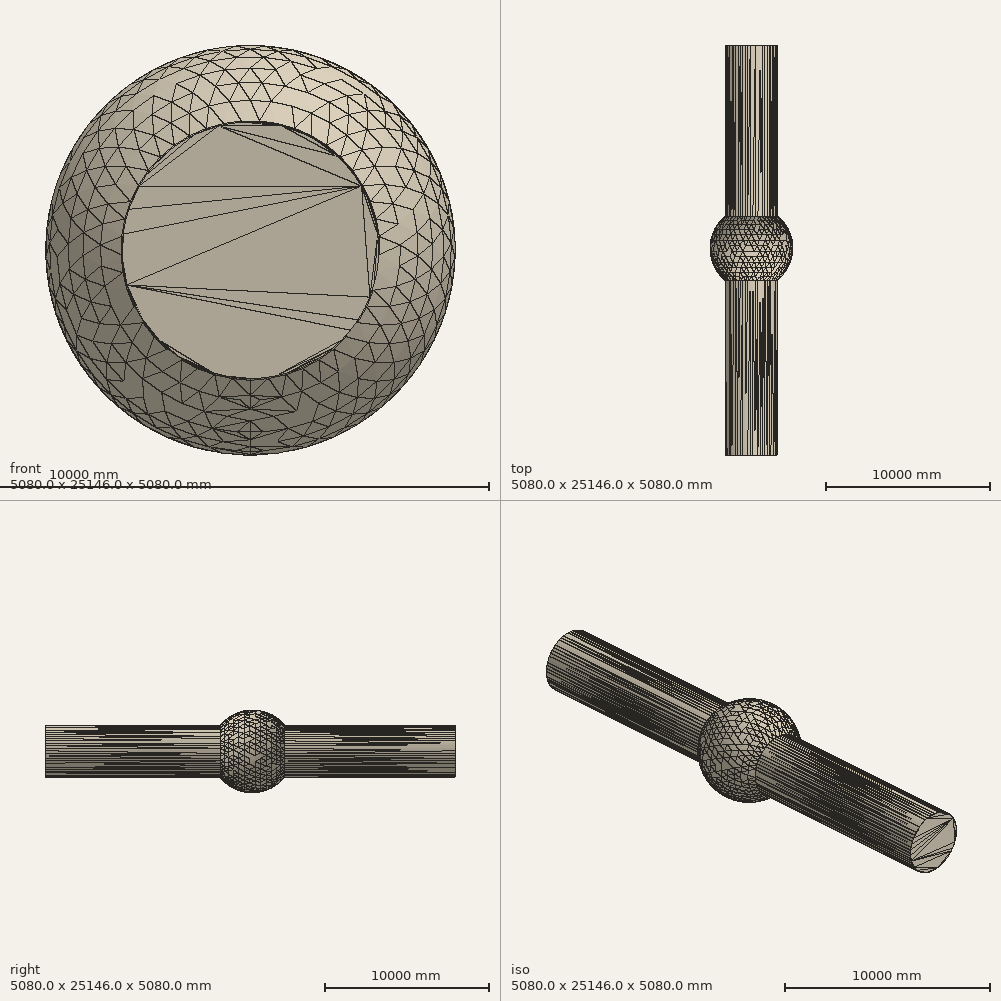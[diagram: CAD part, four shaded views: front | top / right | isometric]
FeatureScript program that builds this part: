
annotation { "Feature Type Name" : "Feature", "Feature Type Description" : "" }
export const myFeature = defineFeature(function(context is Context, id is Id, definition is map)
    precondition{}
    {
        {
            var Q0;
            Q0=qCreatedBy(makeId("Front.planeOp"),FACE);
            var sketch = newSketch(context, id + "F0", { "sketchPlane" : qUnion([Q0])});
            skCircle(sketch, "E0", {"center": v(0, 0) * mm, "radius": 1587.5 * mm});
            skSolve(sketch);
        }
        {
            var Q0;
            Q0 = qSketchRegion(id + "F0", true);
            extrude(context, id + "F1", {"entities" : qUnion([Q0]), "depth" : 10922 * mm, "offsetDistance" : 25.4 * mm});
        }
        {
            var Q0;
            Q0=qCreatedBy(makeId("Right.planeOp"),FACE);
            var sketch = newSketch(context, id + "F2", { "sketchPlane" : qUnion([Q0])});
            skLineSegment(sketch, "E1", {"start": v(0, 0) * mm, "end": v(1778, 0) * mm});
            skArc(sketch, "E2", {"start": v(-762, 0) * mm, "mid": v(1778, -2540) * mm, "end": v(4318, 0) * mm});
            skArc(sketch, "E3", {"start": v(-444.5, 0) * mm, "mid": v(1778, -2222.5) * mm, "end": v(4000.5, 0) * mm});
            skLineSegment(sketch, "E4", {"start": v(-762, 0) * mm, "end": v(4318, 0) * mm});
            skSolve(sketch);
        }
        {
            var Q0;
            {var subQ0=sQuery(id+"F2.wireOp",EDGE,"E2");Q0=makeQuery(id+"F2.imprint","IMPRINT",FACE,{"disambiguationData":[TD([[makeQuery(id+"F2.imprint","IMPRINT",EDGE,{"derivedFrom":subQ0}),1.0]])]});}
            var Q1;
            Q1=sQuery(id+"F2.wireOp",EDGE,"E4");
            revolve(context, id + "F3", {"surfaceOperationType" : NewSurfaceOperationType.NEW, "entities" : qUnion([Q0]), "axis" : qUnion([Q1]), "revolveType" : RevolveType.FULL});
        }
        {
            var Q0;
            Q0=qCreatedBy(makeId("Front.planeOp"),FACE);
            cPlane(context, id + "F4", {"entities" : qUnion([Q0]), "cplaneType" : CPlaneType.OFFSET, "offset" : 3556 * mm, "oppositeDirection" : true, "width" : 152.4 * mm, "height" : 152.4 * mm});
        }
        {
            var Q0;
            Q0=qCreatedBy(id+"F4.planeOp",FACE);
            var sketch = newSketch(context, id + "F5", { "sketchPlane" : qUnion([Q0])});
            skCircle(sketch, "E5", {"center": v(0, 0) * mm, "radius": 1587.5 * mm});
            skSolve(sketch);
        }
        {
            var Q0;
            Q0 = qSketchRegion(id + "F5", true);
            extrude(context, id + "F6", {"entities" : qUnion([Q0]), "oppositeDirection" : true, "depth" : 10668 * mm, "offsetDistance" : 25.4 * mm});
        }
    });
